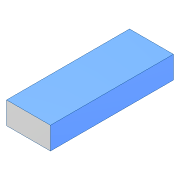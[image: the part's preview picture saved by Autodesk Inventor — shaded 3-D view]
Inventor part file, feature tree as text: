
AUTODESK INVENTOR PART (.ipt)
format: ipt  version: 2022 (Build 260153000, 153)  size: 90,112 bytes
history: native  units: mm
features: extrude x1, sketch x1
ambient origin geometry x8: Origin, YZ Plane, XZ Plane, XY Plane, X Axis, Y Axis, Z Axis, Center Point
bodies: Solid1 (feature_tree)
feature tree (2):
  extrude  "Lipo Body"  Depth=26.0mm
  sketch  "Sketch1"  dims[d0=51.0mm d1=26.0mm d2=143.0mm d3=0.0mm]
